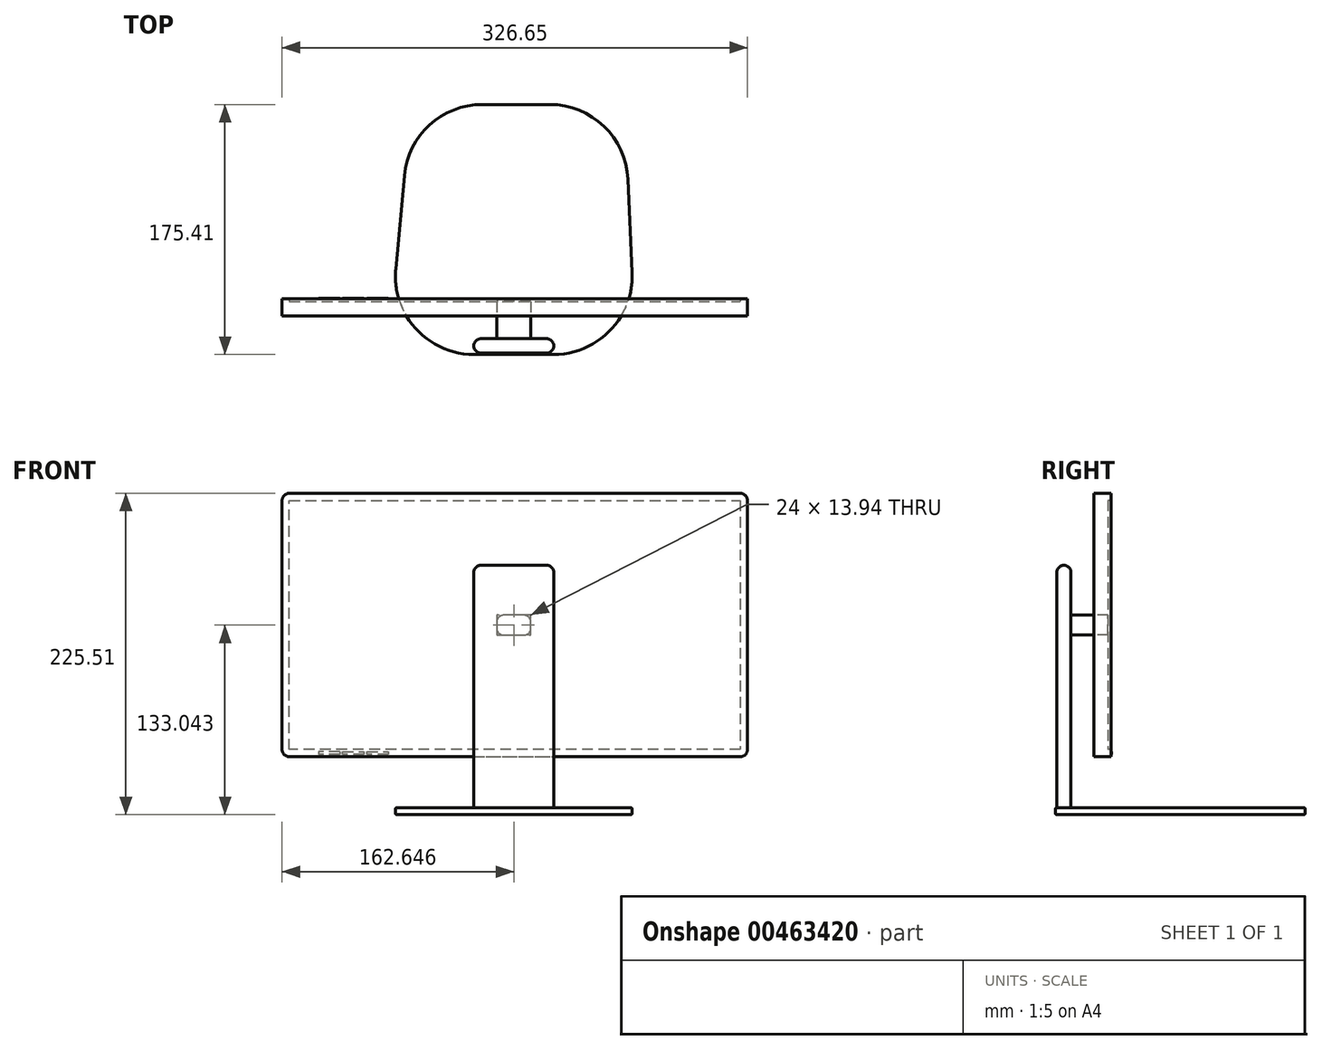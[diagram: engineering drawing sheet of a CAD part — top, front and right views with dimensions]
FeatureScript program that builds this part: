
annotation { "Feature Type Name" : "Feature", "Feature Type Description" : "" }
export const myFeature = defineFeature(function(context is Context, id is Id, definition is map)
    precondition{}
    {
        {
            var Q0;
            Q0=qCreatedBy(makeId("Top.planeOp"),FACE);
            var sketch = newSketch(context, id + "F0", { "sketchPlane" : qUnion([Q0])});
            skLineSegment(sketch, "E0", {"start": v(-23.97, 89.7) * mm, "end": v(23.27, 89.7) * mm});
            skLineSegment(sketch, "E1", {"start": v(-78.74, 39.76) * mm, "end": v(-84.77, -25.64) * mm});
            skLineSegment(sketch, "E2", {"start": v(78.21, 37.16) * mm, "end": v(81.12, -28.25) * mm});
            skLineSegment(sketch, "E3", {"start": v(-30, -85.7) * mm, "end": v(26.18, -85.7) * mm});
            skPoint(sketch, "E4.visualSharp", {"position": v(-74.13, 89.7) * mm});
            skArc(sketch, "E4.filletArc", {"start": v(-23.97, 89.7) * mm, "mid": v(-61.03, 75.35) * mm, "end": v(-78.74, 39.76) * mm});
            skPoint(sketch, "E5.visualSharp", {"position": v(75.87, 89.7) * mm});
            skArc(sketch, "E5.filletArc", {"start": v(78.21, 37.16) * mm, "mid": v(61.28, 74.46) * mm, "end": v(23.27, 89.7) * mm});
            skPoint(sketch, "E6.visualSharp", {"position": v(83.68, -85.7) * mm});
            skArc(sketch, "E6.filletArc", {"start": v(26.18, -85.7) * mm, "mid": v(65.93, -68.71) * mm, "end": v(81.12, -28.25) * mm});
            skPoint(sketch, "E7.visualSharp", {"position": v(-90.32, -85.7) * mm});
            skArc(sketch, "E7.filletArc", {"start": v(-84.77, -25.64) * mm, "mid": v(-70.65, -67.76) * mm, "end": v(-30, -85.7) * mm});
            skSolve(sketch);
        }
        {
            var Q0;
            Q0 = qSketchRegion(id + "F0", true);
            extrude(context, id + "F1", {"entities" : qUnion([Q0]), "depth" : 5 * mm});
        }
        {
            var Q0;
            Q0=makeQuery(id+"F1.opExtrude","CAP_FACE",FACE,{"disambiguationData":[OSD([sQuery(id+"F0.wireOp",EDGE,"E0"),sQuery(id+"F0.wireOp",EDGE,"E1"),sQuery(id+"F0.wireOp",EDGE,"E2"),sQuery(id+"F0.wireOp",EDGE,"E3"),sQuery(id+"F0.wireOp",EDGE,"E4.filletArc"),sQuery(id+"F0.wireOp",EDGE,"E5.filletArc"),sQuery(id+"F0.wireOp",EDGE,"E6.filletArc"),sQuery(id+"F0.wireOp",EDGE,"E7.filletArc")])],"isStart":true});
            var Q1;
            Q1=makeQuery(id+"F1.opExtrude","CAP_EDGE",EDGE,{"disambiguationData":[OSD([sQuery(id+"F0.wireOp",EDGE,"E2")])],"isStart":false});
            var Q2;
            Q2=makeQuery(id+"F1.opExtrude","CAP_FACE",FACE,{"disambiguationData":[OSD([sQuery(id+"F0.wireOp",EDGE,"E0"),sQuery(id+"F0.wireOp",EDGE,"E1"),sQuery(id+"F0.wireOp",EDGE,"E2"),sQuery(id+"F0.wireOp",EDGE,"E3"),sQuery(id+"F0.wireOp",EDGE,"E4.filletArc"),sQuery(id+"F0.wireOp",EDGE,"E5.filletArc"),sQuery(id+"F0.wireOp",EDGE,"E6.filletArc"),sQuery(id+"F0.wireOp",EDGE,"E7.filletArc")])],"isStart":false});
            fillet(context, id + "F2", {"entities" : qUnion([Q0, Q1, Q2]), "radius" : 1 * mm, "tangentPropagation" : true, "allowEdgeOverflow" : false});
        }
        {
            var Q0;
            Q0=makeQuery(id+"F1.opExtrude","CAP_FACE",FACE,{"disambiguationData":[OSD([sQuery(id+"F0.wireOp",EDGE,"E0"),sQuery(id+"F0.wireOp",EDGE,"E1"),sQuery(id+"F0.wireOp",EDGE,"E2"),sQuery(id+"F0.wireOp",EDGE,"E3"),sQuery(id+"F0.wireOp",EDGE,"E4.filletArc"),sQuery(id+"F0.wireOp",EDGE,"E5.filletArc"),sQuery(id+"F0.wireOp",EDGE,"E6.filletArc"),sQuery(id+"F0.wireOp",EDGE,"E7.filletArc")])],"isStart":false});
            var sketch = newSketch(context, id + "F3", { "sketchPlane" : qUnion([Q0])});
            skLineSegment(sketch, "E8", {"start": v(26.18, -84.7) * mm, "end": v(26.18, -74.7) * mm});
            skLineSegment(sketch, "E9", {"start": v(26.18, -74.7) * mm, "end": v(-30, -74.7) * mm});
            skLineSegment(sketch, "E10", {"start": v(-30, -74.7) * mm, "end": v(-30, -84.7) * mm});
            skSolve(sketch);
        }
        {
            var Q0;
            Q0=makeQuery(id+"F3.imprint","IMPRINT",FACE,{"disambiguationData":[TD([[makeQuery(id+"F3.imprint","IMPRINT",EDGE,{"derivedFrom":sQuery(id+"F3.wireOp",EDGE,"E8")}),1.0]])]});
            extrude(context, id + "F4", {"entities" : qUnion([Q0]), "operationType" : NewBodyOperationType.ADD, "depth" : 170 * mm});
        }
        {
            var Q0;
            Q0=makeQuery(id+"F4.opExtrude","SWEPT_EDGE",EDGE,{"disambiguationData":[OSD([sQuery(id+"F0.wireOp",EDGE,"E0"),sQuery(id+"F0.wireOp",EDGE,"E1"),sQuery(id+"F0.wireOp",EDGE,"E2"),sQuery(id+"F0.wireOp",EDGE,"E3"),sQuery(id+"F0.wireOp",EDGE,"E4.filletArc"),sQuery(id+"F0.wireOp",EDGE,"E5.filletArc"),sQuery(id+"F0.wireOp",EDGE,"E6.filletArc"),sQuery(id+"F0.wireOp",EDGE,"E7.filletArc"),sQuery(id+"F3.wireOp",EDGE,"E8")])]});
            fillet(context, id + "F5", {"entities" : qUnion([Q0]), "radius" : 5 * mm, "tangentPropagation" : true, "allowEdgeOverflow" : false});
        }
        {
            var Q0;
            Q0=makeQuery(id+"F4.opExtrude","SWEPT_EDGE",EDGE,{"disambiguationData":[OSD([sQuery(id+"F3.wireOp",EDGE,"E8"),sQuery(id+"F3.wireOp",EDGE,"E9")])]});
            var Q1;
            Q1=makeQuery(id+"F4.opExtrude","SWEPT_EDGE",EDGE,{"disambiguationData":[OSD([sQuery(id+"F3.wireOp",EDGE,"E9"),sQuery(id+"F3.wireOp",EDGE,"E10")])]});
            var Q2;
            Q2=makeQuery(id+"F4.opExtrude","SWEPT_EDGE",EDGE,{"disambiguationData":[OSD([sQuery(id+"F0.wireOp",EDGE,"E0"),sQuery(id+"F0.wireOp",EDGE,"E1"),sQuery(id+"F0.wireOp",EDGE,"E2"),sQuery(id+"F0.wireOp",EDGE,"E3"),sQuery(id+"F0.wireOp",EDGE,"E4.filletArc"),sQuery(id+"F0.wireOp",EDGE,"E5.filletArc"),sQuery(id+"F0.wireOp",EDGE,"E6.filletArc"),sQuery(id+"F0.wireOp",EDGE,"E7.filletArc"),sQuery(id+"F3.wireOp",EDGE,"E10")])]});
            fillet(context, id + "F6", {"entities" : qUnion([Q0, Q1, Q2]), "radius" : 5 * mm, "tangentPropagation" : true, "allowEdgeOverflow" : false});
        }
        {
            var Q0;
            Q0=makeQuery(id+"F4.opExtrude","SWEPT_FACE",FACE,{"disambiguationData":[OSD([sQuery(id+"F3.wireOp",EDGE,"E9")])]});
            var sketch = newSketch(context, id + "F7", { "sketchPlane" : qUnion([Q0])});
            skLineSegment(sketch, "E11", {"start": v(1.91, 140.01) * mm, "end": v(13.91, 140.01) * mm});
            skPoint(sketch, "E11.startSnap0", {"position": v(1.91, 175) * mm});
            skLineSegment(sketch, "E12", {"start": v(13.91, 140.01) * mm, "end": v(13.91, 126.07) * mm});
            skLineSegment(sketch, "E13", {"start": v(13.91, 126.07) * mm, "end": v(-10.09, 126.07) * mm});
            skLineSegment(sketch, "E14", {"start": v(-10.09, 126.07) * mm, "end": v(-10.09, 140.01) * mm});
            skLineSegment(sketch, "E15", {"start": v(-10.09, 140.01) * mm, "end": v(1.91, 140.01) * mm});
            skSolve(sketch);
        }
        {
            var Q0;
            Q0=makeQuery(id+"F7.imprint","IMPRINT",FACE,{"disambiguationData":[TD([[makeQuery(id+"F7.imprint","IMPRINT",EDGE,{"derivedFrom":sQuery(id+"F7.wireOp",EDGE,"E11")}),-1.0]])]});
            extrude(context, id + "F8", {"entities" : qUnion([Q0]), "operationType" : NewBodyOperationType.ADD, "depth" : 16 * mm});
        }
        {
            var Q0;
            Q0=makeQuery(id+"F4.opExtrude","CAP_EDGE",EDGE,{"disambiguationData":[OSD([sQuery(id+"F3.wireOp",EDGE,"E9")])],"isStart":false});
            var Q1;
            Q1=makeQuery(id+"F4.opExtrude","CAP_FACE",FACE,{"disambiguationData":[OSD([sQuery(id+"F0.wireOp",EDGE,"E0"),sQuery(id+"F0.wireOp",EDGE,"E1"),sQuery(id+"F0.wireOp",EDGE,"E2"),sQuery(id+"F0.wireOp",EDGE,"E3"),sQuery(id+"F0.wireOp",EDGE,"E4.filletArc"),sQuery(id+"F0.wireOp",EDGE,"E5.filletArc"),sQuery(id+"F0.wireOp",EDGE,"E6.filletArc"),sQuery(id+"F0.wireOp",EDGE,"E7.filletArc"),sQuery(id+"F3.wireOp",EDGE,"E8"),sQuery(id+"F3.wireOp",EDGE,"E9"),sQuery(id+"F3.wireOp",EDGE,"E10")])],"isStart":false});
            fillet(context, id + "F9", {"entities" : qUnion([Q0, Q1]), "radius" : 5 * mm, "tangentPropagation" : true, "allowEdgeOverflow" : false});
        }
        {
            var Q0;
            Q0=makeQuery(id+"F8.opExtrude","CAP_FACE",FACE,{"disambiguationData":[OSD([sQuery(id+"F7.wireOp",EDGE,"E11"),sQuery(id+"F7.wireOp",EDGE,"E12"),sQuery(id+"F7.wireOp",EDGE,"E13"),sQuery(id+"F7.wireOp",EDGE,"E14"),sQuery(id+"F7.wireOp",EDGE,"E15")])],"isStart":false});
            var sketch = newSketch(context, id + "F10", { "sketchPlane" : qUnion([Q0])});
            skLineSegment(sketch, "E16", {"start": v(1.91, 140.01) * mm, "end": v(1.91, 225.5) * mm});
            skLineSegment(sketch, "E17", {"start": v(-160.06, 40.7) * mm, "end": v(164.56, 40.7) * mm});
            skLineSegment(sketch, "E18", {"start": v(164.56, 40.7) * mm, "end": v(164.56, 225.5) * mm});
            skLineSegment(sketch, "E19", {"start": v(164.56, 225.5) * mm, "end": v(-162.09, 225.5) * mm});
            skLineSegment(sketch, "E20", {"start": v(-162.09, 225.5) * mm, "end": v(-162.09, 40.7) * mm});
            skLineSegment(sketch, "E21", {"start": v(-160.06, 40.7) * mm, "end": v(-162.09, 40.7) * mm});
            skSolve(sketch);
        }
        {
            var Q0;
            Q0=makeQuery(id+"F10.imprint","IMPRINT",FACE,{"disambiguationData":[TD([[makeQuery(id+"F10.imprint","IMPRINT",EDGE,{"derivedFrom":sQuery(id+"F10.wireOp",EDGE,"E17")}),1.0]])]});
            extrude(context, id + "F11", {"entities" : qUnion([Q0]), "depth" : 10 * mm});
        }
        {
            var Q0;
            Q0=makeQuery(id+"F8.opExtrude","CAP_FACE",FACE,{"disambiguationData":[OSD([sQuery(id+"F7.wireOp",EDGE,"E11"),sQuery(id+"F7.wireOp",EDGE,"E12"),sQuery(id+"F7.wireOp",EDGE,"E13"),sQuery(id+"F7.wireOp",EDGE,"E14"),sQuery(id+"F7.wireOp",EDGE,"E15")])],"isStart":false});
            var sketch = newSketch(context, id + "F12", { "sketchPlane" : qUnion([Q0])});
            skSolve(sketch);
        }
        {
            var Q0;
            Q0=makeQuery(id+"F12.imprint","IMPRINT",FACE,{"disambiguationData":[TD([[makeQuery(id+"F12.imprint","IMPRINT",EDGE,{"derivedFrom":makeQuery(id+"F8.opExtrude","CAP_EDGE",EDGE,{"disambiguationData":[OSD([sQuery(id+"F7.wireOp",EDGE,"E12")])],"isStart":false})}),-1.0]])]});
            extrude(context, id + "F13", {"entities" : qUnion([Q0]), "depth" : 10 * mm});
        }
        {
            var Q0;
            Q0=makeQuery(id+"F11.opExtrude","SWEPT_EDGE",EDGE,{"disambiguationData":[OSD([sQuery(id+"F10.wireOp",EDGE,"E19"),sQuery(id+"F10.wireOp",EDGE,"E20")])]});
            fillet(context, id + "F14", {"entities" : qUnion([Q0]), "radius" : 5 * mm, "tangentPropagation" : true, "allowEdgeOverflow" : false});
        }
        {
            var Q0;
            Q0=makeQuery(id+"F11.opExtrude","SWEPT_EDGE",EDGE,{"disambiguationData":[OSD([sQuery(id+"F10.wireOp",EDGE,"E18"),sQuery(id+"F10.wireOp",EDGE,"E19")])]});
            var Q1;
            Q1=makeQuery(id+"F11.opExtrude","SWEPT_EDGE",EDGE,{"disambiguationData":[OSD([sQuery(id+"F10.wireOp",EDGE,"E17"),sQuery(id+"F10.wireOp",EDGE,"E18")])]});
            var Q2;
            Q2=makeQuery(id+"F11.opExtrude","SWEPT_EDGE",EDGE,{"disambiguationData":[OSD([sQuery(id+"F10.wireOp",EDGE,"E20"),sQuery(id+"F10.wireOp",EDGE,"E21")])]});
            fillet(context, id + "F15", {"entities" : qUnion([Q0, Q1, Q2]), "radius" : 5 * mm, "tangentPropagation" : true, "allowEdgeOverflow" : false});
        }
        {
            var Q0;
            Q0=makeQuery(id+"F11.opExtrude","CAP_FACE",FACE,{"disambiguationData":[OSD([sQuery(id+"F7.wireOp",EDGE,"E11"),sQuery(id+"F7.wireOp",EDGE,"E12"),sQuery(id+"F7.wireOp",EDGE,"E13"),sQuery(id+"F7.wireOp",EDGE,"E14"),sQuery(id+"F7.wireOp",EDGE,"E15"),sQuery(id+"F10.wireOp",EDGE,"E17"),sQuery(id+"F10.wireOp",EDGE,"E18"),sQuery(id+"F10.wireOp",EDGE,"E19"),sQuery(id+"F10.wireOp",EDGE,"E20"),sQuery(id+"F10.wireOp",EDGE,"E21")])],"isStart":false});
            var sketch = newSketch(context, id + "F16", { "sketchPlane" : qUnion([Q0])});
            skLineSegment(sketch, "E22", {"start": v(-157.09, 220.5) * mm, "end": v(-157.09, 45.7) * mm});
            skLineSegment(sketch, "E23", {"start": v(-157.09, 45.7) * mm, "end": v(159.56, 45.7) * mm});
            skLineSegment(sketch, "E24", {"start": v(159.56, 45.7) * mm, "end": v(159.56, 220.5) * mm});
            skLineSegment(sketch, "E25", {"start": v(159.56, 220.5) * mm, "end": v(-157.09, 220.5) * mm});
            skSolve(sketch);
        }
        {
            var Q0;
            Q0=makeQuery(id+"F16.imprint","IMPRINT",FACE,{"disambiguationData":[TD([[makeQuery(id+"F16.imprint","IMPRINT",EDGE,{"derivedFrom":sQuery(id+"F16.wireOp",EDGE,"E22")}),-1.0]])]});
            extrude(context, id + "F17", {"entities" : qUnion([Q0]), "operationType" : NewBodyOperationType.ADD, "depth" : 2 * mm});
        }
        {
            var Q0;
            Q0=makeQuery(id+"F17.opExtrude","CAP_FACE",FACE,{"disambiguationData":[OSD([sQuery(id+"F7.wireOp",EDGE,"E11"),sQuery(id+"F7.wireOp",EDGE,"E12"),sQuery(id+"F7.wireOp",EDGE,"E13"),sQuery(id+"F7.wireOp",EDGE,"E14"),sQuery(id+"F7.wireOp",EDGE,"E15"),sQuery(id+"F10.wireOp",EDGE,"E17"),sQuery(id+"F10.wireOp",EDGE,"E18"),sQuery(id+"F10.wireOp",EDGE,"E19"),sQuery(id+"F10.wireOp",EDGE,"E20"),sQuery(id+"F10.wireOp",EDGE,"E21"),sQuery(id+"F16.wireOp",EDGE,"E22"),sQuery(id+"F16.wireOp",EDGE,"E23"),sQuery(id+"F16.wireOp",EDGE,"E24"),sQuery(id+"F16.wireOp",EDGE,"E25")])],"isStart":false});
            var sketch = newSketch(context, id + "F18", { "sketchPlane" : qUnion([Q0])});
            skLineSegment(sketch, "E26", {"start": v(139.1, 44.2) * mm, "end": v(139.1, 42.2) * mm});
            skLineSegment(sketch, "E27", {"start": v(130.46, 42.2) * mm, "end": v(139.1, 42.2) * mm});
            skLineSegment(sketch, "E28", {"start": v(129.1, 44.2) * mm, "end": v(139.1, 44.2) * mm});
            skPoint(sketch, "E29.orphan", {"position": v(139.1, 40.7) * mm});
            skPoint(sketch, "E30.orphan", {"position": v(139.1, 45.7) * mm});
            skPoint(sketch, "E31.start.orphan", {"position": v(139.1, 43.2) * mm});
            skLineSegment(sketch, "E32", {"start": v(129.1, 44.2) * mm, "end": v(124.1, 44.2) * mm});
            skLineSegment(sketch, "E33", {"start": v(124.1, 44.2) * mm, "end": v(124.1, 42.2) * mm});
            skLineSegment(sketch, "E34", {"start": v(124.1, 42.2) * mm, "end": v(130.46, 42.2) * mm});
            skPoint(sketch, "E35.end.orphan", {"position": v(133.92, 43.8) * mm});
            skPoint(sketch, "E36.end.orphan", {"position": v(132.82, 43.8) * mm});
            skLineSegment(sketch, "E37", {"start": v(122.1, 44.2) * mm, "end": v(107.1, 44.2) * mm});
            skLineSegment(sketch, "E38", {"start": v(107.1, 44.2) * mm, "end": v(107.1, 42.2) * mm});
            skLineSegment(sketch, "E39", {"start": v(107.1, 42.2) * mm, "end": v(122.1, 42.2) * mm});
            skLineSegment(sketch, "E40", {"start": v(122.1, 42.2) * mm, "end": v(122.1, 44.2) * mm});
            skLineSegment(sketch, "E41", {"start": v(104.95, 44.2) * mm, "end": v(89.95, 44.2) * mm});
            skLineSegment(sketch, "E42", {"start": v(89.95, 44.2) * mm, "end": v(89.95, 42.2) * mm});
            skLineSegment(sketch, "E43", {"start": v(89.95, 42.2) * mm, "end": v(104.95, 42.2) * mm});
            skLineSegment(sketch, "E44", {"start": v(104.95, 42.2) * mm, "end": v(104.95, 44.2) * mm});
            skSolve(sketch);
        }
        {
            var Q0;
            Q0=makeQuery(id+"F18.imprint","IMPRINT",FACE,{"disambiguationData":[TD([[makeQuery(id+"F18.imprint","IMPRINT",EDGE,{"derivedFrom":sQuery(id+"F18.wireOp",EDGE,"E41")}),1.0]])]});
            var Q1;
            Q1=makeQuery(id+"F18.imprint","IMPRINT",FACE,{"disambiguationData":[TD([[makeQuery(id+"F18.imprint","IMPRINT",EDGE,{"derivedFrom":sQuery(id+"F18.wireOp",EDGE,"E37")}),1.0]])]});
            var Q2;
            Q2=makeQuery(id+"F18.imprint","IMPRINT",FACE,{"disambiguationData":[TD([[makeQuery(id+"F18.imprint","IMPRINT",EDGE,{"derivedFrom":sQuery(id+"F18.wireOp",EDGE,"E26")}),-1.0]])]});
            extrude(context, id + "F19", {"entities" : qUnion([Q0, Q1, Q2]), "operationType" : NewBodyOperationType.ADD, "depth" : 0.5 * mm});
        }
        {
            var Q0;
            Q0=makeQuery(id+"F8.opExtrude","SWEPT_EDGE",EDGE,{"disambiguationData":[OSD([sQuery(id+"F7.wireOp",EDGE,"E11"),sQuery(id+"F7.wireOp",EDGE,"E12")])]});
            fillet(context, id + "F20", {"entities" : qUnion([Q0]), "radius" : 5 * mm, "tangentPropagation" : true, "allowEdgeOverflow" : false});
        }
        {
            var Q0;
            Q0=makeQuery(id+"F8.opExtrude","SWEPT_EDGE",EDGE,{"disambiguationData":[OSD([sQuery(id+"F7.wireOp",EDGE,"E12"),sQuery(id+"F7.wireOp",EDGE,"E13")])]});
            var Q1;
            Q1=makeQuery(id+"F8.opExtrude","SWEPT_EDGE",EDGE,{"disambiguationData":[OSD([sQuery(id+"F7.wireOp",EDGE,"E14"),sQuery(id+"F7.wireOp",EDGE,"E15")])]});
            var Q2;
            Q2=makeQuery(id+"F8.opExtrude","SWEPT_EDGE",EDGE,{"disambiguationData":[OSD([sQuery(id+"F7.wireOp",EDGE,"E13"),sQuery(id+"F7.wireOp",EDGE,"E14")])]});
            fillet(context, id + "F21", {"entities" : qUnion([Q0, Q1, Q2]), "radius" : 5 * mm, "tangentPropagation" : true, "allowEdgeOverflow" : false});
        }
    });
